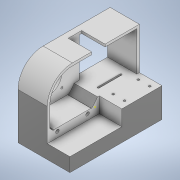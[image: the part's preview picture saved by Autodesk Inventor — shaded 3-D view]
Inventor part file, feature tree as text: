
AUTODESK INVENTOR PART (.ipt)
format: ipt  version: 2022 (Build 260153000, 153)  size: 1,372,672 bytes
history: mixed  units: mm
features: sketch x30, extrude x29, other x3, fillet x1, plane x1, imported_body x1
ambient origin geometry x8: Origin, YZ Plane, XZ Plane, XY Plane, X Axis, Y Axis, Z Axis, Center Point
bodies: Solid1 (imported_parasolid)
feature tree (65):
  other  "Assembly2.iam"
  other  "96Gears_Stage_1_modified.ipt:1"
  other  "96Gears_Stage_2_modified.ipt:1"
  extrude  "Extrusion3"  Depth=3.0mm
  extrude  "Extrusion5"  Depth=18.0mm TaperAngle=0.0deg
  extrude  "Extrusion6"  Depth=6.0mm TaperAngle=0.0deg
  extrude  "Extrusion7"  Depth=10.0mm TaperAngle=0.0deg
  extrude  "Extrusion8"  Depth=4.1mm
  extrude  "Extrusion9"  Depth=7.0mm
  extrude  "Extrusion10"  Depth=50.0mm TaperAngle=0.0deg
  extrude  "Extrusion11"  Depth=50.0mm TaperAngle=0.0deg
  extrude  "Extrusion12"  Depth=3.0mm TaperAngle=0.0deg
  extrude  "Extrusion13"  Depth=3.0mm TaperAngle=0.0deg
  extrude  "Extrusion14"  Depth=3.0mm TaperAngle=0.0deg
  extrude  "Extrusion15"  Depth=9.0mm TaperAngle=0.0deg
  extrude  "Extrusion16"  Depth=30.0mm
  fillet  "Fillet1"  Radius=5.0mm
  extrude  "Extrusion17"  Depth=10.0mm TaperAngle=0.0deg
  extrude  "Extrusion18"  Depth=10.0mm TaperAngle=0.0deg
  extrude  "Extrusion19"  Depth=1.25mm
  extrude  "Extrusion20"  Depth=10.0mm TaperAngle=0.0deg
  extrude  "Extrusion21"  Depth=10.0mm TaperAngle=0.0deg
  extrude  "Extrusion22"  Depth=3.0mm
  plane  "Work Plane1"
  extrude  "Extrusion23"  Depth=10.0mm TaperAngle=0.0deg
  extrude  "Extrusion24"  Depth=10.0mm TaperAngle=0.0deg
  extrude  "Extrusion25"  Depth=10.0mm TaperAngle=0.0deg
  extrude  "Extrusion26"  Depth=10.0mm TaperAngle=0.0deg
  extrude  "Extrusion27"  Depth=10.0mm TaperAngle=0.0deg
  extrude  "Extrusion28"  Depth=16.0mm
  extrude  "Extrusion29"  Depth=10.0mm
  extrude  "Extrusion30"  [1 undecoded]
  extrude  "Extrusion31"  [1 undecoded]
  extrude  "Extrusion32"  [1 undecoded]
  sketch  "Sketch5"  dims[d7=6.0mm d8=18.0mm d9=0.0mm]
  sketch  "Sketch4"  dims[d0=10.0mm d6=3.0mm]
  sketch  "Sketch7"  dims[d17=32.25mm d18=6.0mm d19=0.0mm]
  sketch  "Sketch8"  dims[d20=10.0mm d21=10.0mm d22=0.0mm]
  sketch  "Sketch9"  dims[d24=4.1mm d25=4.1mm]
  sketch  "Sketch10"  dims[d26=10.0mm d27=0.0mm d28=7.0mm]
  sketch  "Sketch11"  dims[d29=0.0mm d30=0.0mm d31=50.0mm d32=0.0mm]
  sketch  "Sketch12"  dims[d33=3.0mm d34=50.0mm d35=0.0mm]
  sketch  "Sketch13"  dims[d38=3.0mm d39=3.0mm d40=0.0mm]
  sketch  "Sketch14"  dims[d41=23.0mm d42=3.0mm d43=0.0mm]
  sketch  "Sketch15"  dims[d44=3.0mm d45=0.0mm d46=9.0mm d47=0.0mm]
  sketch  "Sketch16"  dims[d49=33.25mm d50=9.0mm d51=0.0mm]
  sketch  "Sketch17"  dims[d52=2.0mm d53=0.0mm d54=30.0mm d55=5.0mm]
  sketch  "Sketch18"  dims[d57=5.0mm d58=10.0mm d59=0.0mm]
  sketch  "Sketch19"  dims[d60=3.0mm d61=10.0mm d62=0.0mm]
  sketch  "Sketch20"  dims[d63=2.0mm d64=0.0mm d65=1.25mm]
  sketch  "Sketch21"  dims[d66=2.0mm d67=0.0mm d68=10.0mm d69=0.0mm]
  sketch  "Sketch22"  dims[d74=2.5mm d75=10.0mm d76=0.0mm]
  sketch  "Sketch23"  dims[d80=10.0mm d81=0.0mm d82=3.0mm]
  sketch  "Sketch25"  dims[d83=6.0mm d84=10.0mm d85=0.0mm]
  sketch  "Sketch26"  dims[d94=2.5mm d95=10.0mm d96=0.0mm]
  sketch  "Sketch27"  dims[d97=6.0mm d98=10.0mm d99=0.0mm]
  sketch  "Sketch28"  dims[d100=10.0mm d101=0.0mm d102=10.0mm d103=0.0mm]
  sketch  "Sketch29"  dims[d104=10.0mm d105=0.0mm d106=10.0mm d107=0.0mm]
  sketch  "Sketch30"  dims[d108=8.0mm d109=16.0mm]
  sketch  "Sketch31"  dims[d110=10.0mm d111=0.0mm d112=2.5mm]
  sketch  "Sketch32"  dims[d114=10.0mm d115=0.0mm]
  sketch  "Sketch33"
  sketch  "Sketch34"
  sketch  "Sketch35"
  imported_body  NMx_Import_Brep_tag  [imported B-rep: ~53 faces, bbox_mm=[62.0, 85.0, 110.0]]
note: 3 required parameter values undecoded (feature->parameter linkage not recoverable at this tier; creation-order binding heuristic only, values carry confidence <= 0.55)
